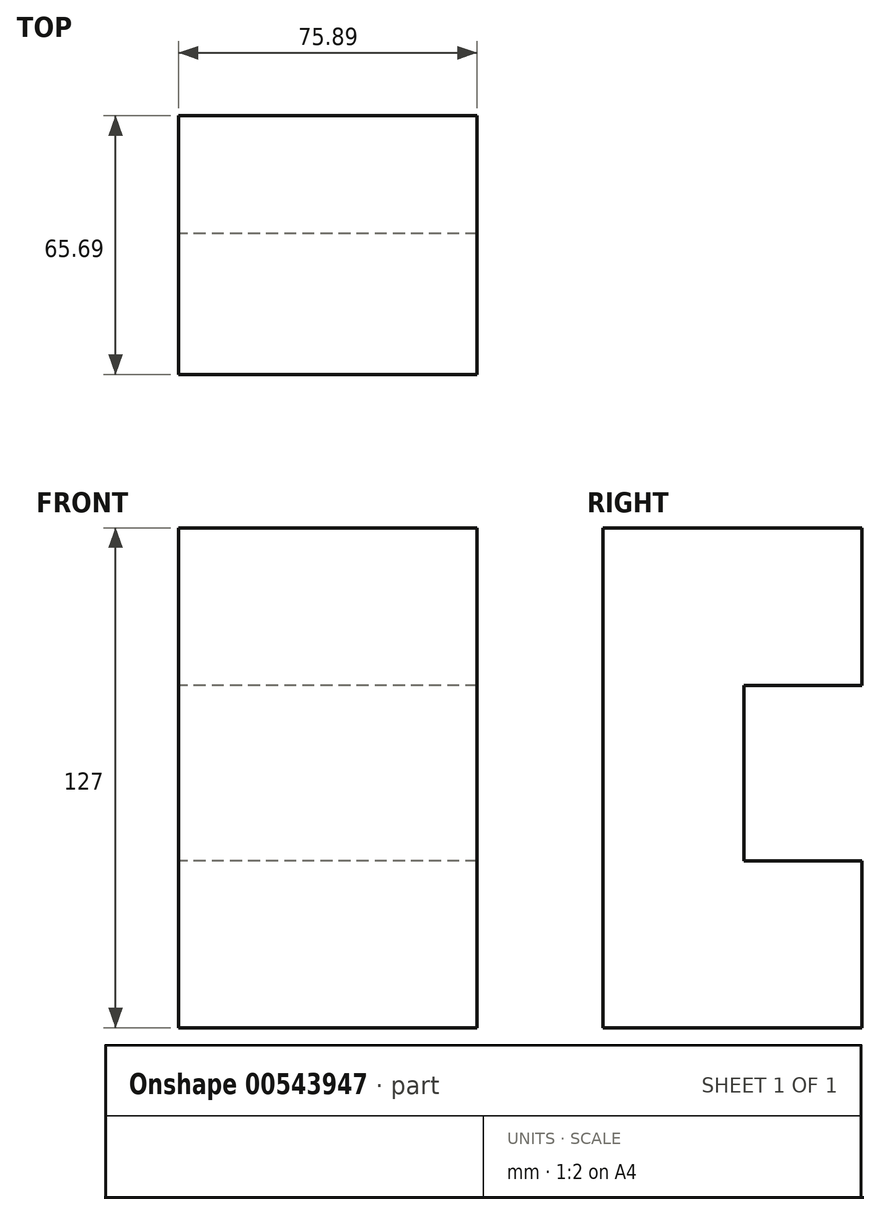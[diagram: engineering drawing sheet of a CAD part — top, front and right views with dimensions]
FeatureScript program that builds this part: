
annotation { "Feature Type Name" : "Feature", "Feature Type Description" : "" }
export const myFeature = defineFeature(function(context is Context, id is Id, definition is map)
    precondition{}
    {
        {
            var Q0;
            Q0=qCreatedBy(makeId("Top.planeOp"),FACE);
            var sketch = newSketch(context, id + "F0", { "sketchPlane" : qUnion([Q0])});
            skLineSegment(sketch, "E0.bottom", {"start": v(-39.03, 29.96) * mm, "end": v(36.86, 29.96) * mm});
            skLineSegment(sketch, "E0.top", {"start": v(-39.03, -35.73) * mm, "end": v(36.86, -35.73) * mm});
            skLineSegment(sketch, "E0.left", {"start": v(-39.03, 29.96) * mm, "end": v(-39.03, -35.73) * mm});
            skLineSegment(sketch, "E0.right", {"start": v(36.86, 29.96) * mm, "end": v(36.86, -35.73) * mm});
            skSolve(sketch);
        }
        {
            var Q0;
            Q0=makeQuery(id+"F0.imprint","IMPRINT",FACE,{"disambiguationData":[TD([[makeQuery(id+"F0.imprint","IMPRINT",EDGE,{"derivedFrom":sQuery(id+"F0.wireOp",EDGE,"E0.bottom")}),-1.0]])]});
            extrude(context, id + "F1", {"entities" : qUnion([Q0]), "depth" : 127 * mm, "offsetDistance" : 25.4 * mm});
        }
        {
            var Q0;
            Q0=makeQuery(id+"F1.opExtrude","SWEPT_FACE",FACE,{"disambiguationData":[OSD([sQuery(id+"F0.wireOp",EDGE,"E0.left")])]});
            var sketch = newSketch(context, id + "F2", { "sketchPlane" : qUnion([Q0])});
            skLineSegment(sketch, "E1.bottom", {"start": v(-29.96, 42.36) * mm, "end": v(0, 42.36) * mm});
            skLineSegment(sketch, "E1.top", {"start": v(-29.96, 86.92) * mm, "end": v(0, 86.92) * mm});
            skLineSegment(sketch, "E1.left", {"start": v(-29.96, 42.36) * mm, "end": v(-29.96, 86.92) * mm});
            skLineSegment(sketch, "E1.right", {"start": v(0, 42.36) * mm, "end": v(0, 86.92) * mm});
            skSolve(sketch);
        }
        {
            var Q0;
            Q0=makeQuery(id+"F2.imprint","IMPRINT",FACE,{"disambiguationData":[TD([[makeQuery(id+"F2.imprint","IMPRINT",EDGE,{"derivedFrom":sQuery(id+"F2.wireOp",EDGE,"E1.bottom")}),1.0]])]});
            extrude(context, id + "F3", {"entities" : qUnion([Q0]), "operationType" : NewBodyOperationType.REMOVE, "oppositeDirection" : true, "depth" : 76.2 * mm, "offsetDistance" : 25.4 * mm});
        }
    });
